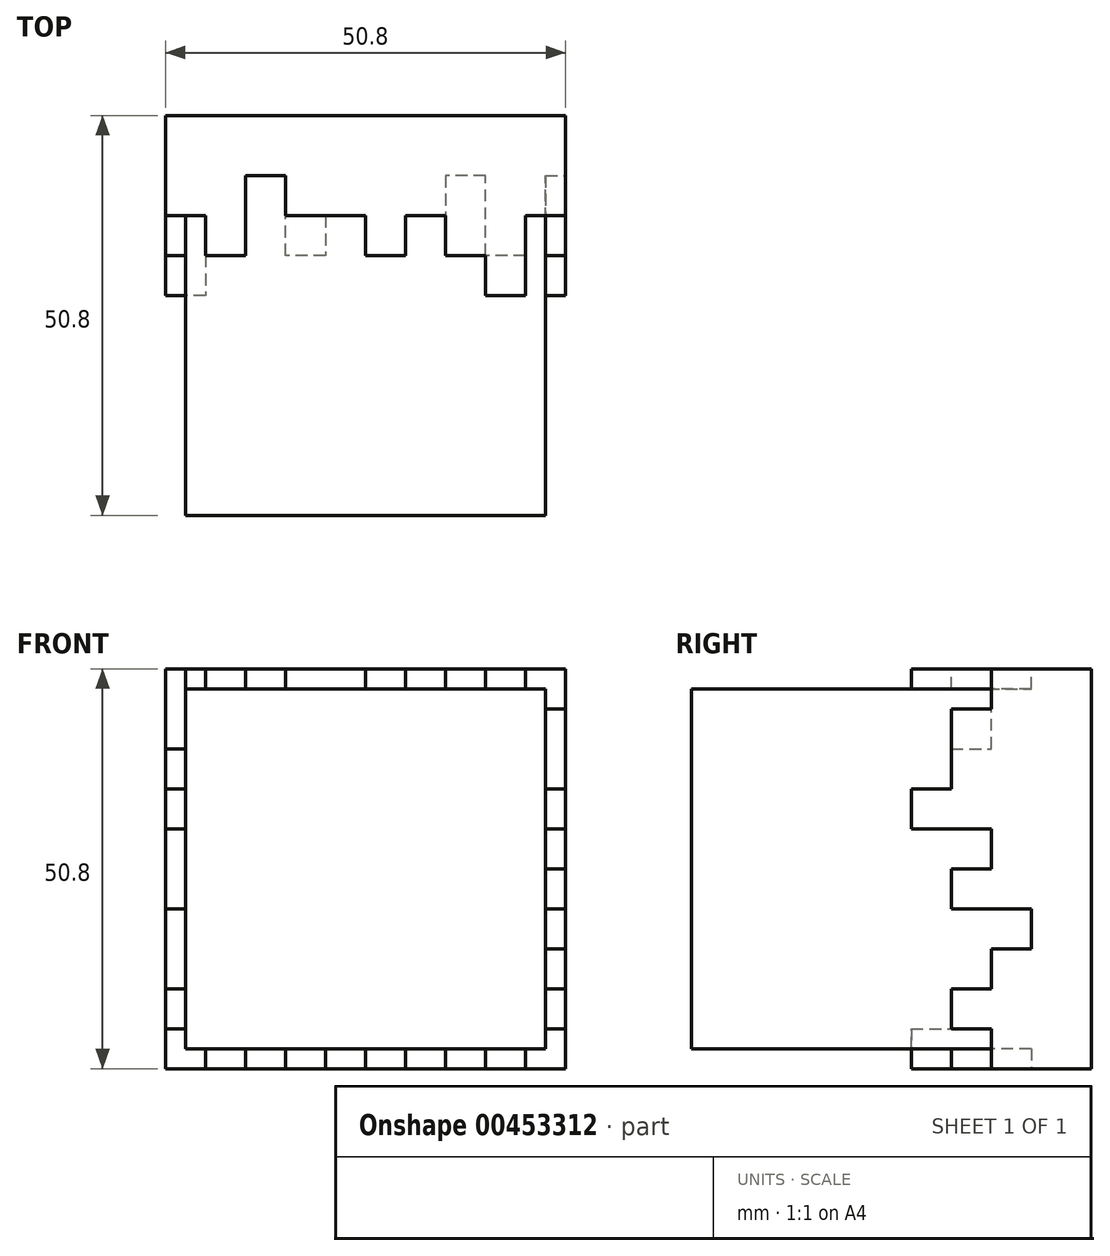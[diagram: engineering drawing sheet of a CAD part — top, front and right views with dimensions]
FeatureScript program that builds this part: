
annotation { "Feature Type Name" : "Feature", "Feature Type Description" : "" }
export const myFeature = defineFeature(function(context is Context, id is Id, definition is map)
    precondition{}
    {
        {
            var Q0;
            Q0=qCreatedBy(makeId("Front.planeOp"),FACE);
            var sketch = newSketch(context, id + "F0", { "sketchPlane" : qUnion([Q0])});
            skLineSegment(sketch, "E0.bottom", {"start": v(20.84, 13.83) * mm, "end": v(-29.96, 13.83) * mm});
            skLineSegment(sketch, "E0.top", {"start": v(20.84, -36.97) * mm, "end": v(-29.96, -36.97) * mm});
            skLineSegment(sketch, "E0.left", {"start": v(20.84, 13.83) * mm, "end": v(20.84, -36.97) * mm});
            skLineSegment(sketch, "E0.right", {"start": v(-29.96, 13.83) * mm, "end": v(-29.96, -36.97) * mm});
            skSolve(sketch);
        }
        {
            var Q0;
            Q0 = qSketchRegion(id + "F0", true);
            var Q1;
            Q1=makeQuery(id+"F0.imprint","IMPRINT",FACE,{"disambiguationData":[TD([[makeQuery(id+"F0.imprint","IMPRINT",EDGE,{"derivedFrom":sQuery(id+"F0.wireOp",EDGE,"E0.bottom")}),1.0]])]});
            extrude(context, id + "F1", {"entities" : qUnion([Q0, Q1]), "depth" : 50.8 * mm});
        }
        {
            var Q0;
            Q0=makeQuery(id+"F1.opExtrude","SWEPT_FACE",FACE,{"disambiguationData":[OSD([sQuery(id+"F0.wireOp",EDGE,"E0.bottom")])]});
            var sketch = newSketch(context, id + "F2", { "sketchPlane" : qUnion([Q0])});
            skLineSegment(sketch, "E1", {"start": v(-29.96, -12.73) * mm, "end": v(-24.88, -12.73) * mm});
            skLineSegment(sketch, "E2", {"start": v(-24.88, -12.73) * mm, "end": v(-24.88, -17.8) * mm});
            skLineSegment(sketch, "E3", {"start": v(-24.88, -17.8) * mm, "end": v(-19.8, -17.8) * mm});
            skLineSegment(sketch, "E4", {"start": v(-19.8, -17.8) * mm, "end": v(-19.8, -7.65) * mm});
            skLineSegment(sketch, "E5", {"start": v(-19.8, -7.65) * mm, "end": v(-14.72, -7.65) * mm});
            skLineSegment(sketch, "E6", {"start": v(-14.72, -7.65) * mm, "end": v(-14.72, -12.73) * mm});
            skLineSegment(sketch, "E7", {"start": v(-14.72, -12.73) * mm, "end": v(-9.64, -12.73) * mm});
            skLineSegment(sketch, "E8", {"start": v(-9.64, -12.73) * mm, "end": v(-4.56, -12.73) * mm});
            skLineSegment(sketch, "E9", {"start": v(-4.56, -12.73) * mm, "end": v(-4.56, -17.8) * mm});
            skLineSegment(sketch, "E10", {"start": v(-4.56, -17.8) * mm, "end": v(0.52, -17.8) * mm});
            skLineSegment(sketch, "E11", {"start": v(0.52, -17.8) * mm, "end": v(0.52, -12.73) * mm});
            skLineSegment(sketch, "E12", {"start": v(0.52, -12.73) * mm, "end": v(5.6, -12.73) * mm});
            skLineSegment(sketch, "E13", {"start": v(5.6, -12.73) * mm, "end": v(5.6, -17.8) * mm});
            skLineSegment(sketch, "E14", {"start": v(5.6, -17.8) * mm, "end": v(10.68, -17.8) * mm});
            skLineSegment(sketch, "E15", {"start": v(10.68, -17.8) * mm, "end": v(10.68, -22.89) * mm});
            skLineSegment(sketch, "E16", {"start": v(10.68, -22.89) * mm, "end": v(15.76, -22.89) * mm});
            skLineSegment(sketch, "E17", {"start": v(15.76, -22.89) * mm, "end": v(15.76, -12.73) * mm});
            skLineSegment(sketch, "E18", {"start": v(15.76, -12.73) * mm, "end": v(20.84, -12.73) * mm});
            skSolve(sketch);
        }
        {
            var Q0;
            {var subQ0=sQuery(id+"F2.wireOp",EDGE,"E1");Q0=makeQuery(id+"F2.imprint","IMPRINT",FACE,{"disambiguationData":[TD([[makeQuery(id+"F2.imprint","IMPRINT",EDGE,{"derivedFrom":subQ0}),-1.0]])]});}
            extrude(context, id + "F3", {"entities" : qUnion([Q0]), "operationType" : NewBodyOperationType.REMOVE, "oppositeDirection" : true, "depth" : 2.54 * mm});
        }
        {
            var Q0;
            Q0=makeQuery(id+"F1.opExtrude","SWEPT_FACE",FACE,{"disambiguationData":[OSD([sQuery(id+"F0.wireOp",EDGE,"E0.left")])]});
            var sketch = newSketch(context, id + "F4", { "sketchPlane" : qUnion([Q0])});
            skLineSegment(sketch, "E19", {"start": v(-12.73, 13.83) * mm, "end": v(-12.73, 8.75) * mm});
            skPoint(sketch, "E19.endSnap0", {"position": v(-12.73, 12.56) * mm});
            skLineSegment(sketch, "E20", {"start": v(-12.73, 8.75) * mm, "end": v(-17.8, 8.75) * mm});
            skLineSegment(sketch, "E21", {"start": v(-17.8, 8.75) * mm, "end": v(-17.8, 3.67) * mm});
            skLineSegment(sketch, "E22", {"start": v(-17.8, 3.67) * mm, "end": v(-17.8, -1.41) * mm});
            skLineSegment(sketch, "E23", {"start": v(-17.8, -1.41) * mm, "end": v(-22.89, -1.41) * mm});
            skLineSegment(sketch, "E24", {"start": v(-22.89, -1.41) * mm, "end": v(-22.89, -6.5) * mm});
            skLineSegment(sketch, "E25", {"start": v(-22.89, -6.5) * mm, "end": v(-12.73, -6.5) * mm});
            skLineSegment(sketch, "E26", {"start": v(-12.73, -6.5) * mm, "end": v(-12.73, -11.57) * mm});
            skLineSegment(sketch, "E27", {"start": v(-12.73, -11.57) * mm, "end": v(-17.8, -11.57) * mm});
            skLineSegment(sketch, "E28", {"start": v(-17.8, -11.57) * mm, "end": v(-17.8, -16.65) * mm});
            skLineSegment(sketch, "E29", {"start": v(-17.8, -16.65) * mm, "end": v(-12.73, -16.65) * mm});
            skLineSegment(sketch, "E30", {"start": v(-12.73, -16.65) * mm, "end": v(-7.65, -16.65) * mm});
            skLineSegment(sketch, "E31", {"start": v(-7.65, -16.65) * mm, "end": v(-7.65, -21.73) * mm});
            skLineSegment(sketch, "E32", {"start": v(-7.65, -21.73) * mm, "end": v(-12.73, -21.73) * mm});
            skLineSegment(sketch, "E33", {"start": v(-12.73, -21.73) * mm, "end": v(-12.73, -26.81) * mm});
            skLineSegment(sketch, "E34", {"start": v(-12.73, -26.81) * mm, "end": v(-17.8, -26.81) * mm});
            skLineSegment(sketch, "E35", {"start": v(-17.8, -26.81) * mm, "end": v(-17.8, -31.9) * mm});
            skLineSegment(sketch, "E36", {"start": v(-17.8, -31.9) * mm, "end": v(-12.73, -31.9) * mm});
            skLineSegment(sketch, "E37", {"start": v(-12.73, -31.9) * mm, "end": v(-12.73, -36.97) * mm});
            skSolve(sketch);
        }
        {
            var Q0;
            {var subQ3=sQuery(id+"F4.wireOp",EDGE,"E20");Q0=makeQuery(id+"F4.imprint","IMPRINT",FACE,{"disambiguationData":[TD([[makeQuery(id+"F4.imprint","IMPRINT",EDGE,{"derivedFrom":subQ3}),-1.0]])]});}
            extrude(context, id + "F5", {"entities" : qUnion([Q0]), "operationType" : NewBodyOperationType.REMOVE, "oppositeDirection" : true, "depth" : 2.54 * mm});
        }
        {
            var Q0;
            Q0=makeQuery(id+"F1.opExtrude","SWEPT_FACE",FACE,{"disambiguationData":[OSD([sQuery(id+"F0.wireOp",EDGE,"E0.top")])]});
            var sketch = newSketch(context, id + "F6", { "sketchPlane" : qUnion([Q0])});
            skLineSegment(sketch, "E38", {"start": v(20.84, 12.73) * mm, "end": v(15.76, 12.73) * mm});
            skPoint(sketch, "E38.endSnap0", {"position": v(19.57, 12.73) * mm});
            skLineSegment(sketch, "E39", {"start": v(15.76, 12.73) * mm, "end": v(15.76, 17.8) * mm});
            skLineSegment(sketch, "E40", {"start": v(15.76, 17.8) * mm, "end": v(10.68, 17.8) * mm});
            skLineSegment(sketch, "E41", {"start": v(10.68, 17.8) * mm, "end": v(10.68, 12.73) * mm});
            skLineSegment(sketch, "E42", {"start": v(10.68, 12.73) * mm, "end": v(10.68, 7.65) * mm});
            skLineSegment(sketch, "E43", {"start": v(10.68, 7.65) * mm, "end": v(5.6, 7.65) * mm});
            skLineSegment(sketch, "E44", {"start": v(5.6, 7.65) * mm, "end": v(5.6, 12.73) * mm});
            skLineSegment(sketch, "E45", {"start": v(5.6, 12.73) * mm, "end": v(0.52, 12.73) * mm});
            skLineSegment(sketch, "E46", {"start": v(0.52, 12.73) * mm, "end": v(0.52, 17.8) * mm});
            skLineSegment(sketch, "E47", {"start": v(0.52, 17.8) * mm, "end": v(-4.56, 17.8) * mm});
            skLineSegment(sketch, "E48", {"start": v(-4.56, 17.8) * mm, "end": v(-4.56, 12.73) * mm});
            skLineSegment(sketch, "E49", {"start": v(-4.56, 12.73) * mm, "end": v(-9.64, 12.73) * mm});
            skLineSegment(sketch, "E50", {"start": v(-9.64, 12.73) * mm, "end": v(-9.64, 17.8) * mm});
            skLineSegment(sketch, "E51", {"start": v(-9.64, 17.8) * mm, "end": v(-14.72, 17.8) * mm});
            skLineSegment(sketch, "E52", {"start": v(-14.72, 17.8) * mm, "end": v(-14.72, 7.65) * mm});
            skLineSegment(sketch, "E53", {"start": v(-14.72, 7.65) * mm, "end": v(-19.8, 7.65) * mm});
            skLineSegment(sketch, "E54", {"start": v(-19.8, 7.65) * mm, "end": v(-19.8, 17.8) * mm});
            skLineSegment(sketch, "E55", {"start": v(-19.8, 17.8) * mm, "end": v(-24.88, 17.8) * mm});
            skLineSegment(sketch, "E56", {"start": v(-24.88, 17.8) * mm, "end": v(-24.88, 22.88) * mm});
            skLineSegment(sketch, "E57", {"start": v(-24.88, 22.88) * mm, "end": v(-29.96, 22.88) * mm});
            skSolve(sketch);
        }
        {
            var Q0;
            {var subQ4=sQuery(id+"F6.wireOp",EDGE,"E39");Q0=makeQuery(id+"F6.imprint","IMPRINT",FACE,{"disambiguationData":[TD([[makeQuery(id+"F6.imprint","IMPRINT",EDGE,{"derivedFrom":subQ4}),-1.0]])]});}
            extrude(context, id + "F7", {"entities" : qUnion([Q0]), "operationType" : NewBodyOperationType.REMOVE, "oppositeDirection" : true, "depth" : 2.54 * mm});
        }
        {
            var Q0;
            Q0=makeQuery(id+"F1.opExtrude","SWEPT_FACE",FACE,{"disambiguationData":[OSD([sQuery(id+"F0.wireOp",EDGE,"E0.right")])]});
            var sketch = newSketch(context, id + "F8", { "sketchPlane" : qUnion([Q0])});
            skLineSegment(sketch, "E58", {"start": v(22.88, -36.97) * mm, "end": v(22.88, -31.9) * mm});
            skLineSegment(sketch, "E59", {"start": v(22.88, -31.9) * mm, "end": v(17.8, -31.9) * mm});
            skLineSegment(sketch, "E60", {"start": v(17.8, -31.9) * mm, "end": v(17.8, -26.81) * mm});
            skLineSegment(sketch, "E61", {"start": v(17.8, -26.81) * mm, "end": v(12.72, -26.81) * mm});
            skLineSegment(sketch, "E62", {"start": v(12.72, -26.81) * mm, "end": v(12.72, -16.65) * mm});
            skLineSegment(sketch, "E63", {"start": v(12.72, -16.65) * mm, "end": v(17.8, -16.65) * mm});
            skLineSegment(sketch, "E64", {"start": v(17.8, -16.65) * mm, "end": v(17.8, -11.57) * mm});
            skLineSegment(sketch, "E65", {"start": v(17.8, -11.57) * mm, "end": v(17.8, -6.5) * mm});
            skLineSegment(sketch, "E66", {"start": v(17.8, -6.5) * mm, "end": v(22.88, -6.5) * mm});
            skLineSegment(sketch, "E67", {"start": v(22.88, -6.5) * mm, "end": v(22.88, -1.41) * mm});
            skLineSegment(sketch, "E68", {"start": v(22.88, -1.41) * mm, "end": v(17.8, -1.41) * mm});
            skLineSegment(sketch, "E69", {"start": v(17.8, -1.41) * mm, "end": v(17.8, 3.67) * mm});
            skLineSegment(sketch, "E70", {"start": v(17.8, 3.67) * mm, "end": v(12.72, 3.67) * mm});
            skLineSegment(sketch, "E71", {"start": v(12.72, 3.67) * mm, "end": v(12.73, 13.83) * mm});
            skSolve(sketch);
        }
        {
            var Q0;
            {var subQ3=sQuery(id+"F8.wireOp",EDGE,"E59");Q0=makeQuery(id+"F8.imprint","IMPRINT",FACE,{"disambiguationData":[TD([[makeQuery(id+"F8.imprint","IMPRINT",EDGE,{"derivedFrom":subQ3}),-1.0]])]});}
            extrude(context, id + "F9", {"entities" : qUnion([Q0]), "operationType" : NewBodyOperationType.REMOVE, "oppositeDirection" : true, "depth" : 2.54 * mm});
        }
    });
